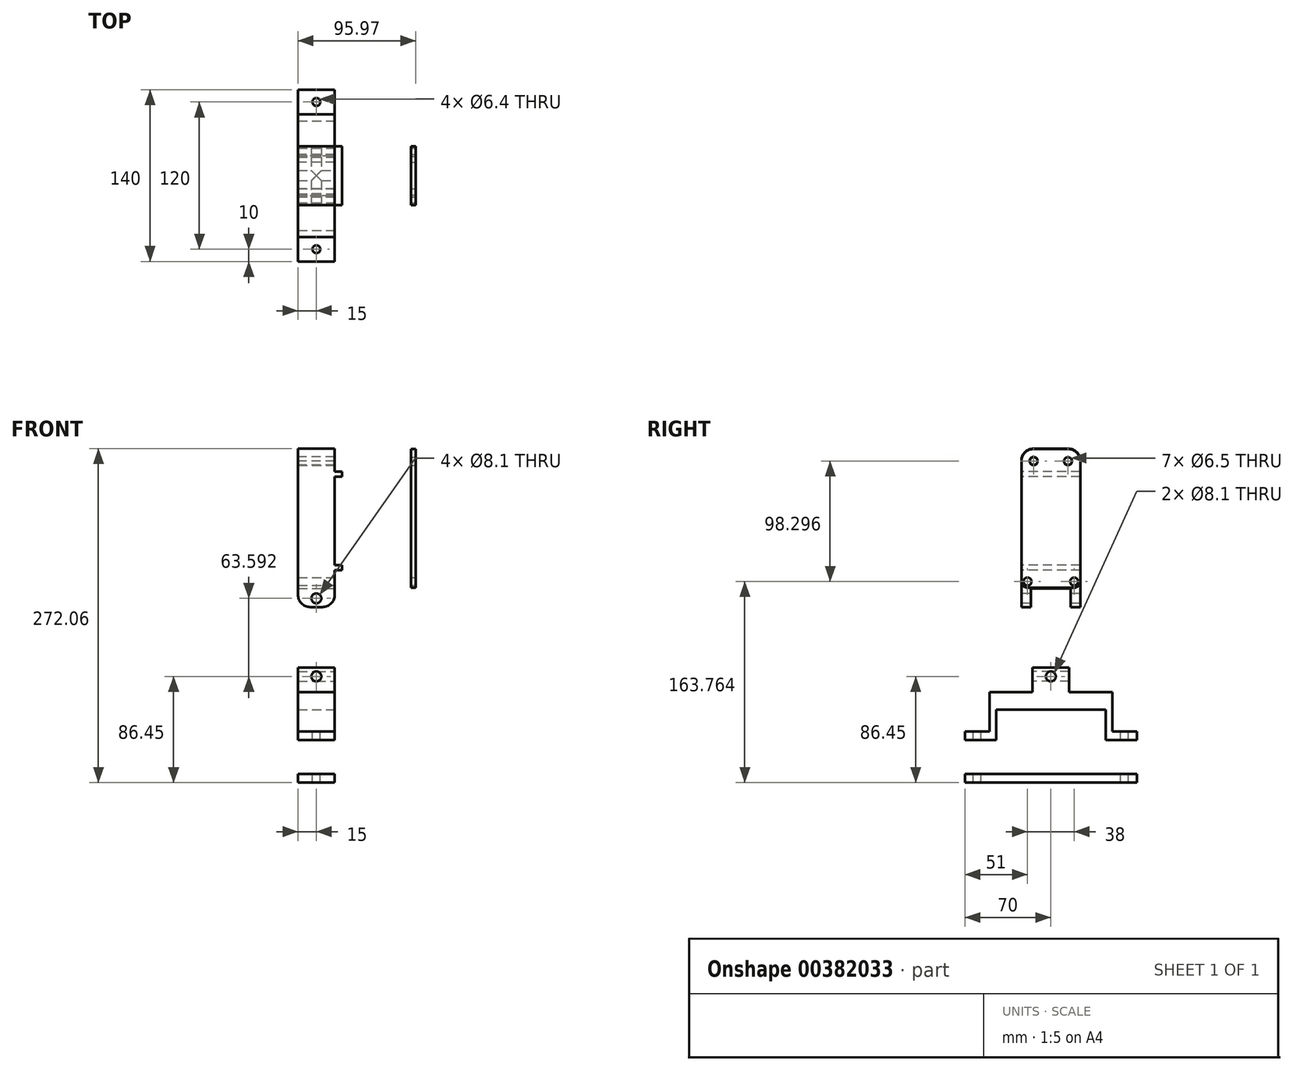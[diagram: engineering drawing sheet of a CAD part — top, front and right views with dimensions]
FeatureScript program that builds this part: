
annotation { "Feature Type Name" : "Feature", "Feature Type Description" : "" }
export const myFeature = defineFeature(function(context is Context, id is Id, definition is map)
    precondition{}
    {
        {
            var Q0;
            Q0=qCreatedBy(makeId("Top.planeOp"),FACE);
            var sketch = newSketch(context, id + "F0", { "sketchPlane" : qUnion([Q0])});
            skLineSegment(sketch, "E0.bottom", {"start": v(-15, -50) * mm, "end": v(15, -50) * mm});
            skLineSegment(sketch, "E0.top", {"start": v(-15, 50) * mm, "end": v(15, 50) * mm});
            skLineSegment(sketch, "E0.left", {"start": v(-15, -50) * mm, "end": v(-15, 50) * mm});
            skLineSegment(sketch, "E0.right", {"start": v(15, -50) * mm, "end": v(15, 50) * mm});
            skPoint(sketch, "E0.middle", {"position": v(0, 0) * mm});
            skSolve(sketch);
        }
        {
            var Q0;
            Q0 = qSketchRegion(id + "F0", true);
            extrude(context, id + "F1", {"entities" : qUnion([Q0]), "depth" : 70 * mm});
        }
        {
            var Q0;
            Q0=makeQuery(id+"F1.opExtrude","CAP_FACE",FACE,{"disambiguationData":[OSD([sQuery(id+"F0.wireOp",EDGE,"E0.bottom"),sQuery(id+"F0.wireOp",EDGE,"E0.top"),sQuery(id+"F0.wireOp",EDGE,"E0.left"),sQuery(id+"F0.wireOp",EDGE,"E0.right")])],"isStart":false});
            var sketch = newSketch(context, id + "F2", { "sketchPlane" : qUnion([Q0])});
            skLineSegment(sketch, "E1.bottom", {"start": v(-15, -15) * mm, "end": v(15, -15) * mm});
            skLineSegment(sketch, "E1.top", {"start": v(-15, 15) * mm, "end": v(15, 15) * mm});
            skLineSegment(sketch, "E1.left", {"start": v(-15, -15) * mm, "end": v(-15, 15) * mm});
            skLineSegment(sketch, "E1.right", {"start": v(15, -15) * mm, "end": v(15, 15) * mm});
            skPoint(sketch, "E1.middle", {"position": v(0, 0) * mm});
            skSolve(sketch);
        }
        {
            var Q0;
            Q0 = qSketchRegion(id + "F2", true);
            extrude(context, id + "F3", {"entities" : qUnion([Q0]), "operationType" : NewBodyOperationType.ADD, "depth" : 20 * mm});
        }
        {
            var Q0;
            Q0=qCreatedBy(makeId("Right.planeOp"),FACE);
            var sketch = newSketch(context, id + "F4", { "sketchPlane" : qUnion([Q0])});
            skLineSegment(sketch, "E2.bottom", {"start": v(24, 154.5) * mm, "end": v(-24, 154.5) * mm});
            skLineSegment(sketch, "E2.top", {"start": v(24, 178.56) * mm, "end": v(-24, 178.56) * mm});
            skLineSegment(sketch, "E2.left", {"start": v(24, 154.5) * mm, "end": v(24, 178.56) * mm});
            skLineSegment(sketch, "E2.right", {"start": v(-24, 154.5) * mm, "end": v(-24, 178.56) * mm});
            skPoint(sketch, "E2.middle", {"position": v(0, 166.53) * mm});
            skSolve(sketch);
        }
        {
            var Q0;
            Q0 = qSketchRegion(id + "F4", true);
            extrude(context, id + "F5", {"entities" : qUnion([Q0]), "endBound" : BoundingType.SYMMETRIC, "depth" : 30 * mm});
        }
        {
            var Q0;
            Q0=makeQuery(id+"F5.opExtrude","SWEPT_FACE",FACE,{"disambiguationData":[OSD([sQuery(id+"F4.wireOp",EDGE,"E2.bottom")])]});
            var sketch = newSketch(context, id + "F6", { "sketchPlane" : qUnion([Q0])});
            skLineSegment(sketch, "E3.bottom", {"start": v(-15, -24) * mm, "end": v(15, -24) * mm});
            skLineSegment(sketch, "E3.top", {"start": v(-15, -16.16) * mm, "end": v(15, -16.16) * mm});
            skLineSegment(sketch, "E3.left", {"start": v(-15, -24) * mm, "end": v(-15, -16.16) * mm});
            skLineSegment(sketch, "E3.right", {"start": v(15, -24) * mm, "end": v(15, -16.16) * mm});
            skPoint(sketch, "E3.middle", {"position": v(0, -20.09) * mm});
            skPoint(sketch, "E3.middle.positionSnap0", {"position": v(0, -24) * mm});
            skPoint(sketch, "E3.centerSnap0", {"position": v(0, -24) * mm});
            skSolve(sketch);
        }
        {
            var Q0;
            Q0 = qSketchRegion(id + "F6", true);
            extrude(context, id + "F7", {"entities" : qUnion([Q0]), "operationType" : NewBodyOperationType.ADD, "depth" : 15 * mm});
        }
        {
            var Q0;
            Q0=makeQuery(id+"F5.opExtrude","SWEPT_FACE",FACE,{"disambiguationData":[OSD([sQuery(id+"F4.wireOp",EDGE,"E2.bottom")])]});
            var sketch = newSketch(context, id + "F8", { "sketchPlane" : qUnion([Q0])});
            skLineSegment(sketch, "E4.bottom", {"start": v(-15, 16.16) * mm, "end": v(15, 16.16) * mm});
            skLineSegment(sketch, "E4.top", {"start": v(-15, 24) * mm, "end": v(15, 24) * mm});
            skLineSegment(sketch, "E4.left", {"start": v(-15, 16.16) * mm, "end": v(-15, 24) * mm});
            skLineSegment(sketch, "E4.right", {"start": v(15, 16.16) * mm, "end": v(15, 24) * mm});
            skPoint(sketch, "E4.middle", {"position": v(0, 20.09) * mm});
            skPoint(sketch, "E4.middle.positionSnap0", {"position": v(0, 24) * mm});
            skPoint(sketch, "E4.centerSnap0", {"position": v(0, 24) * mm});
            skSolve(sketch);
        }
        {
            var Q0;
            Q0 = qSketchRegion(id + "F8", true);
            extrude(context, id + "F9", {"entities" : qUnion([Q0]), "operationType" : NewBodyOperationType.ADD, "depth" : 15 * mm});
        }
        {
            var Q0;
            Q0=makeQuery(id+"F9.opExtrude","CAP_EDGE",EDGE,{"disambiguationData":[OSD([sQuery(id+"F8.wireOp",EDGE,"E4.right")])],"isStart":false});
            fillet(context, id + "F10", {"entities" : qUnion([Q0]), "radius" : 10 * mm, "tangentPropagation" : true, "allowEdgeOverflow" : false});
        }
        {
            var Q0;
            Q0=makeQuery(id+"F9.opExtrude","CAP_EDGE",EDGE,{"disambiguationData":[OSD([sQuery(id+"F8.wireOp",EDGE,"E4.left")])],"isStart":false});
            fillet(context, id + "F11", {"entities" : qUnion([Q0]), "radius" : 10 * mm, "tangentPropagation" : true, "allowEdgeOverflow" : false});
        }
        {
            var Q0;
            Q0=makeQuery(id+"F7.opExtrude","CAP_EDGE",EDGE,{"disambiguationData":[OSD([sQuery(id+"F6.wireOp",EDGE,"E3.right")])],"isStart":false});
            fillet(context, id + "F12", {"entities" : qUnion([Q0]), "radius" : 10 * mm, "tangentPropagation" : true, "allowEdgeOverflow" : false});
        }
        {
            var Q0;
            Q0=makeQuery(id+"F7.opExtrude","CAP_EDGE",EDGE,{"disambiguationData":[OSD([sQuery(id+"F6.wireOp",EDGE,"E3.left")])],"isStart":false});
            fillet(context, id + "F13", {"entities" : qUnion([Q0]), "radius" : 10 * mm, "tangentPropagation" : true, "allowEdgeOverflow" : false});
        }
        {
            var Q0;
            Q0=makeQuery(id+"F3.opExtrude","SWEPT_FACE",FACE,{"disambiguationData":[OSD([sQuery(id+"F2.wireOp",EDGE,"E1.bottom")])]});
            var sketch = newSketch(context, id + "F14", { "sketchPlane" : qUnion([Q0])});
            skCircle(sketch, "E5", {"center": v(0, 82.95) * mm, "radius": 4.05 * mm});
            skPoint(sketch, "E5.centerSnap0", {"position": v(0, 90) * mm});
            skSolve(sketch);
        }
        {
            var Q0;
            Q0 = qSketchRegion(id + "F14", true);
            extrude(context, id + "F15", {"entities" : qUnion([Q0]), "operationType" : NewBodyOperationType.REMOVE, "oppositeDirection" : true, "depth" : 31.5 * mm});
        }
        {
            var Q0;
            Q0=makeQuery(id+"F9.boolean.opBoolean","MERGE",FACE,{"derivedFrom":[makeQuery(id+"F5.opExtrude","SWEPT_FACE",FACE,{"disambiguationData":[OSD([sQuery(id+"F4.wireOp",EDGE,"E2.right")])]}),makeQuery(id+"F9.opExtrude","SWEPT_FACE",FACE,{"disambiguationData":[OSD([sQuery(id+"F8.wireOp",EDGE,"E4.top")])]})]});
            var sketch = newSketch(context, id + "F16", { "sketchPlane" : qUnion([Q0])});
            skCircle(sketch, "E6", {"center": v(0, 146.54) * mm, "radius": 4.05 * mm});
            skPoint(sketch, "E6.centerSnap0", {"position": v(0, 139.5) * mm});
            skSolve(sketch);
        }
        {
            var Q0;
            Q0 = qSketchRegion(id + "F16", true);
            extrude(context, id + "F17", {"entities" : qUnion([Q0]), "operationType" : NewBodyOperationType.REMOVE, "oppositeDirection" : true, "depth" : 49.5 * mm});
        }
        {
            var Q0;
            Q0=makeQuery(id+"F5.opExtrude","SWEPT_FACE",FACE,{"disambiguationData":[OSD([sQuery(id+"F4.wireOp",EDGE,"E2.top")])]});
            var sketch = newSketch(context, id + "F18", { "sketchPlane" : qUnion([Q0])});
            skLineSegment(sketch, "E7.bottom", {"start": v(-15, 24) * mm, "end": v(15, 24) * mm});
            skLineSegment(sketch, "E7.top", {"start": v(-15, -24) * mm, "end": v(15, -24) * mm});
            skLineSegment(sketch, "E7.left", {"start": v(-15, 24) * mm, "end": v(-15, -24) * mm});
            skLineSegment(sketch, "E7.right", {"start": v(15, 24) * mm, "end": v(15, -24) * mm});
            skPoint(sketch, "E7.middle", {"position": v(0, 0) * mm});
            skSolve(sketch);
        }
        {
            var Q0;
            Q0 = qSketchRegion(id + "F18", true);
            extrude(context, id + "F19", {"entities" : qUnion([Q0]), "operationType" : NewBodyOperationType.ADD, "depth" : 90 * mm});
        }
        {
            var Q0;
            Q0=makeQuery(id+"F19.opExtrude","CAP_EDGE",EDGE,{"disambiguationData":[OSD([sQuery(id+"F18.wireOp",EDGE,"E7.bottom")])],"isStart":false});
            fillet(context, id + "F20", {"entities" : qUnion([Q0]), "radius" : 10 * mm, "tangentPropagation" : true, "allowEdgeOverflow" : false});
        }
        {
            var Q0;
            Q0=makeQuery(id+"F19.opExtrude","CAP_EDGE",EDGE,{"disambiguationData":[OSD([sQuery(id+"F18.wireOp",EDGE,"E7.top")])],"isStart":false});
            fillet(context, id + "F21", {"entities" : qUnion([Q0]), "radius" : 10 * mm, "tangentPropagation" : true, "allowEdgeOverflow" : false});
        }
        {
            var Q0;
            Q0=makeQuery(id+"F19.boolean.opBoolean","MERGE",FACE,{"derivedFrom":[makeQuery(id+"F9.boolean.opBoolean","MERGE",FACE,{"derivedFrom":[makeQuery(id+"F7.boolean.opBoolean","MERGE",FACE,{"derivedFrom":[makeQuery(id+"F5.opExtrude","CAP_FACE",FACE,{"disambiguationData":[OSD([sQuery(id+"F4.wireOp",EDGE,"E2.bottom"),sQuery(id+"F4.wireOp",EDGE,"E2.top"),sQuery(id+"F4.wireOp",EDGE,"E2.left"),sQuery(id+"F4.wireOp",EDGE,"E2.right")])],"isStart":false}),makeQuery(id+"F7.opExtrude","SWEPT_FACE",FACE,{"disambiguationData":[OSD([sQuery(id+"F6.wireOp",EDGE,"E3.right")])]})]}),makeQuery(id+"F9.opExtrude","SWEPT_FACE",FACE,{"disambiguationData":[OSD([sQuery(id+"F8.wireOp",EDGE,"E4.right")])]})]}),makeQuery(id+"F19.opExtrude","SWEPT_FACE",FACE,{"disambiguationData":[OSD([sQuery(id+"F18.wireOp",EDGE,"E7.right")])]})]});
            var sketch = newSketch(context, id + "F22", { "sketchPlane" : qUnion([Q0])});
            skLineSegment(sketch, "E8.bottom", {"start": v(24, 245.82) * mm, "end": v(-24, 245.82) * mm});
            skLineSegment(sketch, "E8.top", {"start": v(24, 249.82) * mm, "end": v(-24, 249.82) * mm});
            skLineSegment(sketch, "E8.left", {"start": v(24, 245.82) * mm, "end": v(24, 249.82) * mm});
            skLineSegment(sketch, "E8.right", {"start": v(-24, 245.82) * mm, "end": v(-24, 249.82) * mm});
            skPoint(sketch, "E8.middle", {"position": v(0, 247.82) * mm});
            skPoint(sketch, "E8.middle.positionSnap0", {"position": v(0, 268.56) * mm});
            skPoint(sketch, "E8.centerSnap0", {"position": v(0, 268.56) * mm});
            skLineSegment(sketch, "E9.bottom", {"start": v(24, 169.62) * mm, "end": v(-24, 169.62) * mm});
            skLineSegment(sketch, "E9.top", {"start": v(24, 173.62) * mm, "end": v(-24, 173.62) * mm});
            skLineSegment(sketch, "E9.left", {"start": v(24, 169.62) * mm, "end": v(24, 173.62) * mm});
            skLineSegment(sketch, "E9.right", {"start": v(-24, 169.62) * mm, "end": v(-24, 173.62) * mm});
            skPoint(sketch, "E9.middle", {"position": v(0, 171.62) * mm});
            skSolve(sketch);
        }
        {
            var Q0;
            Q0 = qSketchRegion(id + "F22", true);
            extrude(context, id + "F23", {"entities" : qUnion([Q0]), "operationType" : NewBodyOperationType.ADD, "depth" : 6 * mm});
        }
        {
            var Q0;
            Q0=qCreatedBy(makeId("Front.planeOp"),FACE);
            var sketch = newSketch(context, id + "F24", { "sketchPlane" : qUnion([Q0])});
            skLineSegment(sketch, "E10.bottom", {"start": v(76.97, 268.26) * mm, "end": v(80.97, 268.26) * mm});
            skLineSegment(sketch, "E10.top", {"start": v(76.97, 155.26) * mm, "end": v(80.97, 155.26) * mm});
            skLineSegment(sketch, "E10.left", {"start": v(76.97, 268.26) * mm, "end": v(76.97, 155.26) * mm});
            skLineSegment(sketch, "E10.right", {"start": v(80.97, 268.26) * mm, "end": v(80.97, 155.26) * mm});
            skSolve(sketch);
        }
        {
            var Q0;
            Q0 = qSketchRegion(id + "F24", true);
            extrude(context, id + "F25", {"entities" : qUnion([Q0]), "endBound" : BoundingType.SYMMETRIC, "depth" : 48 * mm});
        }
        {
            var Q0;
            Q0=makeQuery(id+"F25.opExtrude","CAP_EDGE",EDGE,{"disambiguationData":[OSD([sQuery(id+"F24.wireOp",EDGE,"E10.bottom")])],"isStart":false});
            fillet(context, id + "F26", {"entities" : qUnion([Q0]), "radius" : 10 * mm, "tangentPropagation" : true, "allowEdgeOverflow" : false});
        }
        {
            var Q0;
            Q0=makeQuery(id+"F25.opExtrude","CAP_EDGE",EDGE,{"disambiguationData":[OSD([sQuery(id+"F24.wireOp",EDGE,"E10.bottom")])],"isStart":true});
            fillet(context, id + "F27", {"entities" : qUnion([Q0]), "radius" : 10 * mm, "tangentPropagation" : true, "allowEdgeOverflow" : false});
        }
        {
            var Q0;
            Q0=makeQuery(id+"F25.opExtrude","SWEPT_FACE",FACE,{"disambiguationData":[OSD([sQuery(id+"F24.wireOp",EDGE,"E10.right")])]});
            var sketch = newSketch(context, id + "F28", { "sketchPlane" : qUnion([Q0])});
            skCircle(sketch, "E11", {"center": v(-14, 258.26) * mm, "radius": 3.25 * mm});
            skSolve(sketch);
        }
        {
            var Q0;
            Q0 = qSketchRegion(id + "F28", true);
            extrude(context, id + "F29", {"entities" : qUnion([Q0]), "operationType" : NewBodyOperationType.REMOVE, "endBound" : BoundingType.THROUGH_ALL, "oppositeDirection" : true, "depth" : 134 * mm});
        }
        {
            var Q0;
            Q0=makeQuery(id+"F25.opExtrude","CAP_EDGE",EDGE,{"disambiguationData":[OSD([sQuery(id+"F24.wireOp",EDGE,"E10.top")])],"isStart":false});
            fillet(context, id + "F30", {"entities" : qUnion([Q0]), "radius" : 5 * mm, "tangentPropagation" : true, "allowEdgeOverflow" : false});
        }
        {
            var Q0;
            Q0=makeQuery(id+"F25.opExtrude","CAP_EDGE",EDGE,{"disambiguationData":[OSD([sQuery(id+"F24.wireOp",EDGE,"E10.top")])],"isStart":true});
            fillet(context, id + "F31", {"entities" : qUnion([Q0]), "radius" : 5 * mm, "tangentPropagation" : true, "allowEdgeOverflow" : false});
        }
        {
            var Q0;
            Q0=makeQuery(id+"F19.boolean.opBoolean","MERGE",FACE,{"derivedFrom":[makeQuery(id+"F9.boolean.opBoolean","MERGE",FACE,{"derivedFrom":[makeQuery(id+"F7.boolean.opBoolean","MERGE",FACE,{"derivedFrom":[makeQuery(id+"F5.opExtrude","CAP_FACE",FACE,{"disambiguationData":[OSD([sQuery(id+"F4.wireOp",EDGE,"E2.bottom"),sQuery(id+"F4.wireOp",EDGE,"E2.top"),sQuery(id+"F4.wireOp",EDGE,"E2.left"),sQuery(id+"F4.wireOp",EDGE,"E2.right")])],"isStart":true}),makeQuery(id+"F7.opExtrude","SWEPT_FACE",FACE,{"disambiguationData":[OSD([sQuery(id+"F6.wireOp",EDGE,"E3.left")])]})]}),makeQuery(id+"F9.opExtrude","SWEPT_FACE",FACE,{"disambiguationData":[OSD([sQuery(id+"F8.wireOp",EDGE,"E4.left")])]})]}),makeQuery(id+"F19.opExtrude","SWEPT_FACE",FACE,{"disambiguationData":[OSD([sQuery(id+"F18.wireOp",EDGE,"E7.left")])]})]});
            var sketch = newSketch(context, id + "F32", { "sketchPlane" : qUnion([Q0])});
            skCircle(sketch, "E12", {"center": v(-14, 258.56) * mm, "radius": 3.25 * mm});
            skCircle(sketch, "E13", {"center": v(14, 258.56) * mm, "radius": 3.25 * mm});
            skSolve(sketch);
        }
        {
            var Q0;
            Q0 = qSketchRegion(id + "F32", true);
            extrude(context, id + "F33", {"entities" : qUnion([Q0]), "operationType" : NewBodyOperationType.REMOVE, "oppositeDirection" : true, "depth" : 34.6 * mm});
        }
        {
            var Q0;
            Q0=makeQuery(id+"F25.opExtrude","SWEPT_FACE",FACE,{"disambiguationData":[OSD([sQuery(id+"F24.wireOp",EDGE,"E10.right")])]});
            var sketch = newSketch(context, id + "F34", { "sketchPlane" : qUnion([Q0])});
            skCircle(sketch, "E14", {"center": v(14, 258.26) * mm, "radius": 3.25 * mm});
            skSolve(sketch);
        }
        {
            var Q0;
            Q0 = qSketchRegion(id + "F34", true);
            extrude(context, id + "F35", {"entities" : qUnion([Q0]), "operationType" : NewBodyOperationType.REMOVE, "oppositeDirection" : true, "depth" : 25 * mm});
        }
        {
            var Q0;
            Q0=makeQuery(id+"F25.opExtrude","SWEPT_FACE",FACE,{"disambiguationData":[OSD([sQuery(id+"F24.wireOp",EDGE,"E10.right")])]});
            var sketch = newSketch(context, id + "F36", { "sketchPlane" : qUnion([Q0])});
            skCircle(sketch, "E15", {"center": v(-19, 160.26) * mm, "radius": 3.25 * mm});
            skSolve(sketch);
        }
        {
            var Q0;
            Q0 = qSketchRegion(id + "F36", true);
            extrude(context, id + "F37", {"entities" : qUnion([Q0]), "operationType" : NewBodyOperationType.REMOVE, "oppositeDirection" : true, "depth" : 108.8 * mm});
        }
        {
            var Q0;
            Q0=makeQuery(id+"F25.opExtrude","SWEPT_FACE",FACE,{"disambiguationData":[OSD([sQuery(id+"F24.wireOp",EDGE,"E10.right")])]});
            var sketch = newSketch(context, id + "F38", { "sketchPlane" : qUnion([Q0])});
            skCircle(sketch, "E16", {"center": v(19, 160.26) * mm, "radius": 3.25 * mm});
            skSolve(sketch);
        }
        {
            var Q0;
            Q0 = qSketchRegion(id + "F38", true);
            extrude(context, id + "F39", {"entities" : qUnion([Q0]), "operationType" : NewBodyOperationType.REMOVE, "endBound" : BoundingType.THROUGH_ALL, "oppositeDirection" : true, "depth" : 120.1 * mm});
        }
        {
            var Q0;
            Q0=makeQuery(id+"F1.opExtrude","CAP_FACE",FACE,{"disambiguationData":[OSD([sQuery(id+"F0.wireOp",EDGE,"E0.bottom"),sQuery(id+"F0.wireOp",EDGE,"E0.top"),sQuery(id+"F0.wireOp",EDGE,"E0.left"),sQuery(id+"F0.wireOp",EDGE,"E0.right")])],"isStart":true});
            var sketch = newSketch(context, id + "F40", { "sketchPlane" : qUnion([Q0])});
            skLineSegment(sketch, "E17.bottom", {"start": v(-15, -50) * mm, "end": v(15, -50) * mm});
            skLineSegment(sketch, "E17.top", {"start": v(-15, 50) * mm, "end": v(15, 50) * mm});
            skLineSegment(sketch, "E17.left", {"start": v(-15, -50) * mm, "end": v(-15, 50) * mm});
            skLineSegment(sketch, "E17.right", {"start": v(15, -50) * mm, "end": v(15, 50) * mm});
            skPoint(sketch, "E17.middle", {"position": v(0, 0) * mm});
            skSolve(sketch);
        }
        {
            var Q0;
            Q0 = qSketchRegion(id + "F40", true);
            extrude(context, id + "F41", {"entities" : qUnion([Q0]), "operationType" : NewBodyOperationType.REMOVE, "oppositeDirection" : true, "depth" : 31 * mm});
        }
        {
            var Q0;
            Q0=makeQuery(id+"F1.opExtrude","SWEPT_FACE",FACE,{"disambiguationData":[OSD([sQuery(id+"F0.wireOp",EDGE,"E0.top")])]});
            var sketch = newSketch(context, id + "F42", { "sketchPlane" : qUnion([Q0])});
            skLineSegment(sketch, "E18.bottom", {"start": v(-15, 38) * mm, "end": v(15, 38) * mm});
            skLineSegment(sketch, "E18.top", {"start": v(-15, 31) * mm, "end": v(15, 31) * mm});
            skLineSegment(sketch, "E18.left", {"start": v(-15, 38) * mm, "end": v(-15, 31) * mm});
            skLineSegment(sketch, "E18.right", {"start": v(15, 38) * mm, "end": v(15, 31) * mm});
            skSolve(sketch);
        }
        {
            var Q0;
            Q0 = qSketchRegion(id + "F42", true);
            extrude(context, id + "F43", {"entities" : qUnion([Q0]), "operationType" : NewBodyOperationType.ADD, "depth" : 20 * mm});
        }
        {
            var Q0;
            Q0=makeQuery(id+"F1.opExtrude","SWEPT_FACE",FACE,{"disambiguationData":[OSD([sQuery(id+"F0.wireOp",EDGE,"E0.bottom")])]});
            var sketch = newSketch(context, id + "F44", { "sketchPlane" : qUnion([Q0])});
            skLineSegment(sketch, "E19.bottom", {"start": v(-15, 38) * mm, "end": v(15, 38) * mm});
            skLineSegment(sketch, "E19.top", {"start": v(-15, 31) * mm, "end": v(15, 31) * mm});
            skLineSegment(sketch, "E19.left", {"start": v(-15, 38) * mm, "end": v(-15, 31) * mm});
            skLineSegment(sketch, "E19.right", {"start": v(15, 38) * mm, "end": v(15, 31) * mm});
            skSolve(sketch);
        }
        {
            var Q0;
            Q0 = qSketchRegion(id + "F44", true);
            extrude(context, id + "F45", {"entities" : qUnion([Q0]), "operationType" : NewBodyOperationType.ADD, "depth" : 20 * mm});
        }
        {
            var Q0;
            Q0=makeQuery(id+"F43.opExtrude","SWEPT_FACE",FACE,{"disambiguationData":[OSD([sQuery(id+"F42.wireOp",EDGE,"E18.bottom")])]});
            var sketch = newSketch(context, id + "F46", { "sketchPlane" : qUnion([Q0])});
            skCircle(sketch, "E20", {"center": v(0, 60) * mm, "radius": 3.2 * mm});
            skPoint(sketch, "E20.centerSnap0", {"position": v(15, 60) * mm});
            skSolve(sketch);
        }
        {
            var Q0;
            Q0=makeQuery(id+"F45.opExtrude","SWEPT_FACE",FACE,{"disambiguationData":[OSD([sQuery(id+"F44.wireOp",EDGE,"E19.bottom")])]});
            var sketch = newSketch(context, id + "F47", { "sketchPlane" : qUnion([Q0])});
            skCircle(sketch, "E21", {"center": v(0, -60) * mm, "radius": 3.2 * mm});
            skPoint(sketch, "E21.centerSnap0", {"position": v(-15, -60) * mm});
            skSolve(sketch);
        }
        {
            var Q0;
            Q0=qCreatedBy(makeId("Right.planeOp"),FACE);
            var sketch = newSketch(context, id + "F48", { "sketchPlane" : qUnion([Q0])});
            skLineSegment(sketch, "E22.bottom", {"start": v(70, -3.5) * mm, "end": v(-70, -3.5) * mm});
            skLineSegment(sketch, "E22.top", {"start": v(70, 3.5) * mm, "end": v(-70, 3.5) * mm});
            skLineSegment(sketch, "E22.left", {"start": v(70, -3.5) * mm, "end": v(70, 3.5) * mm});
            skLineSegment(sketch, "E22.right", {"start": v(-70, -3.5) * mm, "end": v(-70, 3.5) * mm});
            skPoint(sketch, "E22.middle", {"position": v(0, 0) * mm});
            skSolve(sketch);
        }
        {
            var Q0;
            Q0 = qSketchRegion(id + "F48", true);
            extrude(context, id + "F49", {"entities" : qUnion([Q0]), "endBound" : BoundingType.SYMMETRIC, "depth" : 30 * mm});
        }
        {
            var Q0;
            Q0 = qSketchRegion(id + "F47", true);
            extrude(context, id + "F50", {"entities" : qUnion([Q0]), "operationType" : NewBodyOperationType.REMOVE, "oppositeDirection" : true, "depth" : 55.5 * mm});
        }
        {
            var Q0;
            Q0 = qSketchRegion(id + "F46", true);
            extrude(context, id + "F51", {"entities" : qUnion([Q0]), "operationType" : NewBodyOperationType.REMOVE, "oppositeDirection" : true, "depth" : 61.8 * mm});
        }
        {
            var Q0;
            Q0=makeQuery(id+"F45.boolean.opBoolean","MERGE",FACE,{"derivedFrom":[makeQuery(id+"F43.boolean.opBoolean","MERGE",FACE,{"derivedFrom":[makeQuery(id+"F41.boolean.opBoolean","COPY",FACE,{"derivedFrom":makeQuery(id+"F41.opExtrude","CAP_FACE",FACE,{"disambiguationData":[OSD([sQuery(id+"F40.wireOp",EDGE,"E17.bottom"),sQuery(id+"F40.wireOp",EDGE,"E17.top"),sQuery(id+"F40.wireOp",EDGE,"E17.left"),sQuery(id+"F40.wireOp",EDGE,"E17.right")])],"isStart":false})}),makeQuery(id+"F43.opExtrude","SWEPT_FACE",FACE,{"disambiguationData":[OSD([sQuery(id+"F42.wireOp",EDGE,"E18.top")])]})]}),makeQuery(id+"F45.opExtrude","SWEPT_FACE",FACE,{"disambiguationData":[OSD([sQuery(id+"F44.wireOp",EDGE,"E19.top")])]})]});
            var sketch = newSketch(context, id + "F52", { "sketchPlane" : qUnion([Q0])});
            skLineSegment(sketch, "E23.bottom", {"start": v(-15, -44.59) * mm, "end": v(15, -44.59) * mm});
            skLineSegment(sketch, "E23.top", {"start": v(-15, 44.59) * mm, "end": v(15, 44.59) * mm});
            skLineSegment(sketch, "E23.left", {"start": v(-15, -44.59) * mm, "end": v(-15, 44.59) * mm});
            skLineSegment(sketch, "E23.right", {"start": v(15, -44.59) * mm, "end": v(15, 44.59) * mm});
            skPoint(sketch, "E23.middle", {"position": v(0, 0) * mm});
            skSolve(sketch);
        }
        {
            var Q0;
            Q0 = qSketchRegion(id + "F52", true);
            extrude(context, id + "F53", {"entities" : qUnion([Q0]), "operationType" : NewBodyOperationType.REMOVE, "oppositeDirection" : true, "depth" : 25 * mm});
        }
        {
            var Q0;
            Q0=makeQuery(id+"F45.boolean.opBoolean","MERGE",FACE,{"derivedFrom":[makeQuery(id+"F43.boolean.opBoolean","MERGE",FACE,{"derivedFrom":[makeQuery(id+"F3.boolean.opBoolean","MERGE",FACE,{"derivedFrom":[makeQuery(id+"F1.opExtrude","SWEPT_FACE",FACE,{"disambiguationData":[OSD([sQuery(id+"F0.wireOp",EDGE,"E0.right")])]}),makeQuery(id+"F3.opExtrude","SWEPT_FACE",FACE,{"disambiguationData":[OSD([sQuery(id+"F2.wireOp",EDGE,"E1.right")])]})]}),makeQuery(id+"F43.opExtrude","SWEPT_FACE",FACE,{"disambiguationData":[OSD([sQuery(id+"F42.wireOp",EDGE,"E18.left")])]})]}),makeQuery(id+"F45.opExtrude","SWEPT_FACE",FACE,{"disambiguationData":[OSD([sQuery(id+"F44.wireOp",EDGE,"E19.right")])]})]});
            var sketch = newSketch(context, id + "F54", { "sketchPlane" : qUnion([Q0])});
            skCircle(sketch, "E24", {"center": v(0, 82.95) * mm, "radius": 4.05 * mm});
            skPoint(sketch, "E24.centerSnap0", {"position": v(0, 90) * mm});
            skSolve(sketch);
        }
        {
            var Q0;
            Q0 = qSketchRegion(id + "F54", true);
            extrude(context, id + "F55", {"entities" : qUnion([Q0]), "operationType" : NewBodyOperationType.REMOVE, "oppositeDirection" : true, "depth" : 32.4 * mm});
        }
    });
